# Revit family: RN 81022 Optipress-Aquaplus-Schiebemuffe
name_source: partatom
category: Rohrformteile
units: mm (PartAtom-declared; Revit-internal decimal feet)

## family parameters
Arbeitsebenenbasiert = Nein
Beim Laden mit Abzugskörper schneiden = Nein
Bemaßung runder Anschluss = Durchmesser verwenden
Gemeinsam genutzt = Nein
Immer vertikal = Ja
Teiletyp = Verbindung

## types (7) — shared parameters
1.010.00.2 Blattnummer der Richtlinie = 29
1.010.00.3 Ausgabedatum (Monat) der Richtlinie = 201308
1.010.00.4 Herstellername = R. Nussbaum AG
1.010.00.5 Revisionsdatum der Datei = 20190521
1.010.00.6 Webadresse des Herstellers = http://www.nussbaum.ch
1.100.00.4 Produktbezeichnung = Versorgung
1.110.00.2 Index = 4
1.110.00.4 Produktbezeichnung = Optipress
1.960/3L.00.8 Link (URL) = https://www.nussbaum.ch
29.700.00.4 Produktname = Optipress-Aquaplus-Schiebemuffe
29.700.00.5 Produktkennung = 2
29.700.00.6 Querschnittsform = 1
29.700.00.7 Nennweitensystem = DN
29.700.00.8 Nenndrucksystem = PN
29.710.02.4 Nenndruck = 16
29.710.02.5 max. zul. Überdruck [hPa] = 1600
29.710.02.7 max. zul. Dauer-Betriebsdruck [hPa] = 1600
Connector Visibility = Nein
EnclosingSpace Visibility = Nein

## per-type parameters (varying)
| type | 1.800.00.3 TGA-Nummer | 1.810.00.3 Hersteller-Bestellnummer | 1.810.00.4 DATANORM-Nummer | 1.810.00.5 StLB-Nummer | 1.810.00.6 GTIN-Nummer | 29.710.02.10 Formstück-Gewicht [kg] | 29.710.02.3 Benennung | CONNECTOR0_DIAMETER_dX_0r | CONNECTOR0_dX_00 | CONNECTOR0_dX_01 | CONNECTOR0_ref_dX | CONNECTOR1_DIAMETER_dX_0r | CONNECTOR1_dX_00 | CONNECTOR1_dX_01 | CONNECTOR1_ref_dX | R. Nussbaum AG 81022.22 de Visibility | R. Nussbaum AG 81022.23 de Visibility | R. Nussbaum AG 81022.24 de Visibility | R. Nussbaum AG 81022.25 de Visibility | R. Nussbaum AG 81022.26 de Visibility | R. Nussbaum AG 81022.27 de Visibility | R. Nussbaum AG 81022.28 de Visibility |
| 81022.22, Optipress-Aquaplus-Schiebemuffe, DN=12, L=80 | 01900400000000000000000000000000000000000000000016000000000000000011 | 81022.22 | 81022.22 | 265.212 | 7612945021236 | 0.081 | Optipress-Aquaplus-Schiebemuffe, DN=12, L=80 | 12 mm  [stored 0.0393701 ft] | 40 mm | 18 mm | 18 mm | 12 mm  [stored 0.0393701 ft] | 18 mm | 40 mm | 18 mm | Ja | Nein | Nein | Nein | Nein | Nein | Nein |
| 81022.23, Optipress-Aquaplus-Schiebemuffe, DN=15, L=80 | 01900400000000000000000000000000000000000000000016000000000000000012 | 81022.23 | 81022.23 | 265.213 | 7612945021243 | 0.094 | Optipress-Aquaplus-Schiebemuffe, DN=15, L=80 | 15 mm | 40 mm | 18 mm | 18 mm | 15 mm | 18 mm | 40 mm | 18 mm | Nein | Ja | Nein | Nein | Nein | Nein | Nein |
| 81022.24, Optipress-Aquaplus-Schiebemuffe, DN=20, L=85 | 01900400000000000000000000000000000000000000000016000000000000000013 | 81022.24 | 81022.24 | 265.214 | 7612945021250 | 0.123 | Optipress-Aquaplus-Schiebemuffe, DN=20, L=85 | 20 mm | 43 mm | 19 mm | 19 mm | 20 mm | 19 mm | 43 mm | 19 mm | Nein | Nein | Ja | Nein | Nein | Nein | Nein |
| 81022.25, Optipress-Aquaplus-Schiebemuffe, DN=25, L=95 | 01900400000000000000000000000000000000000000000016000000000000000014 | 81022.25 | 81022.25 | 265.215 | 7612945021267 | 0.17 | Optipress-Aquaplus-Schiebemuffe, DN=25, L=95 | 25 mm  [stored 0.082021 ft] | 48 mm | 24 mm | 24 mm | 25 mm  [stored 0.082021 ft] | 24 mm | 48 mm | 24 mm | Nein | Nein | Nein | Ja | Nein | Nein | Nein |
| 81022.26, Optipress-Aquaplus-Schiebemuffe, DN=32, L=105 | 01900400000000000000000000000000000000000000000016000000000000000015 | 81022.26 | 81022.26 | 265.216 | 7612945021274 | 0.229 | Optipress-Aquaplus-Schiebemuffe, DN=32, L=105 | 32 mm | 53 mm | 27 mm | 27 mm | 32 mm | 27 mm | 53 mm | 27 mm | Nein | Nein | Nein | Nein | Ja | Nein | Nein |
| 81022.27, Optipress-Aquaplus-Schiebemuffe, DN=40, L=120 | 01900400000000000000000000000000000000000000000016000000000000000016 | 81022.27 | 81022.27 | 265.217 | 7612945021281 | 0.381 | Optipress-Aquaplus-Schiebemuffe, DN=40, L=120 | 40 mm | 60 mm | 24 mm | 24 mm | 40 mm | 24 mm | 60 mm | 24 mm | Nein | Nein | Nein | Nein | Nein | Ja | Nein |
| 81022.28, Optipress-Aquaplus-Schiebemuffe, DN=50, L=135 | 01900400000000000000000000000000000000000000000016000000000000000017 | 81022.28 | 81022.28 | 265.218 | 7612945021298 | 0.62 | Optipress-Aquaplus-Schiebemuffe, DN=50, L=135 | 50 mm | 68 mm | 28 mm | 28 mm | 50 mm | 28 mm | 68 mm | 28 mm | Nein | Nein | Nein | Nein | Nein | Nein | Ja |

note: column(s) folded — value = type name in every type: 1.800.00.4 Kommentarfeld

note: [stored X ft] marks values corroborated as IEEE doubles in the binary element streams (Revit-internal decimal feet)

## geometry (parser evidence)
native form markers: Sweep x3
no freeform markers — native parametric forms only
